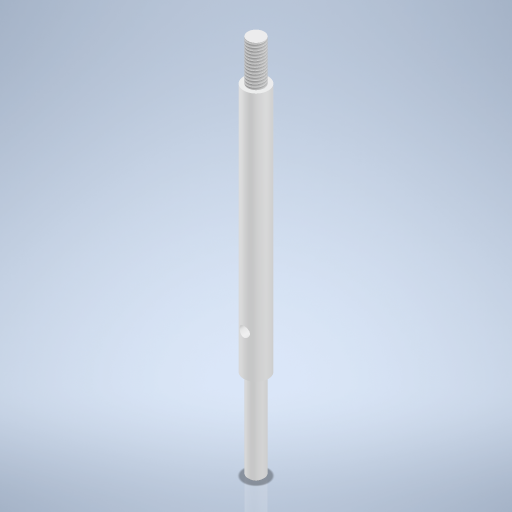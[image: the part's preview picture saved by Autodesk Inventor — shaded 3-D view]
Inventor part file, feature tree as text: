
AUTODESK INVENTOR PART (.ipt)
format: ipt  version: 2024 (Build 280153000, 153)  size: 266,240 bytes
history: native  units: mm
features: sketch x2, revolve x1, thread x1, plane x1, hole x1, chamfer x1, projected_geometry x1
ambient origin geometry x8: Origin, YZ Plane, XZ Plane, XY Plane, X Axis, Y Axis, Z Axis, Center Point
bodies: Volumenkörper1 (feature_tree)
feature tree (8):
  revolve  "Umdrehung1"
  thread  "Gewinde1"  [1 undecoded]
  plane  "Arbeitsebene1"
  hole  "Bohrung1"  [1 undecoded]
  chamfer  "Fasen1"  Distance=6.0mm
  sketch  "Skizze1"  dims[d1=22.0mm d2=93.0mm]
  sketch  "Skizze2"  dims[d3=4.0mm d4=6.0mm d5=90.0deg d6=10.0mm d7=0.0mm d8=3.0mm d9=10.0mm d10=2.5mm d11=6.0mm d12=4.0mm d13=2.0mm d14=90.0deg d15=8.0mm d16=20.594885mm d17=0.5mm d18=2.0mm d19=45.0deg]
  projected_geometry  "Projizierte Kontur1"
note: 2 required parameter values undecoded (feature->parameter linkage not recoverable at this tier; creation-order binding heuristic only, values carry confidence <= 0.55)
